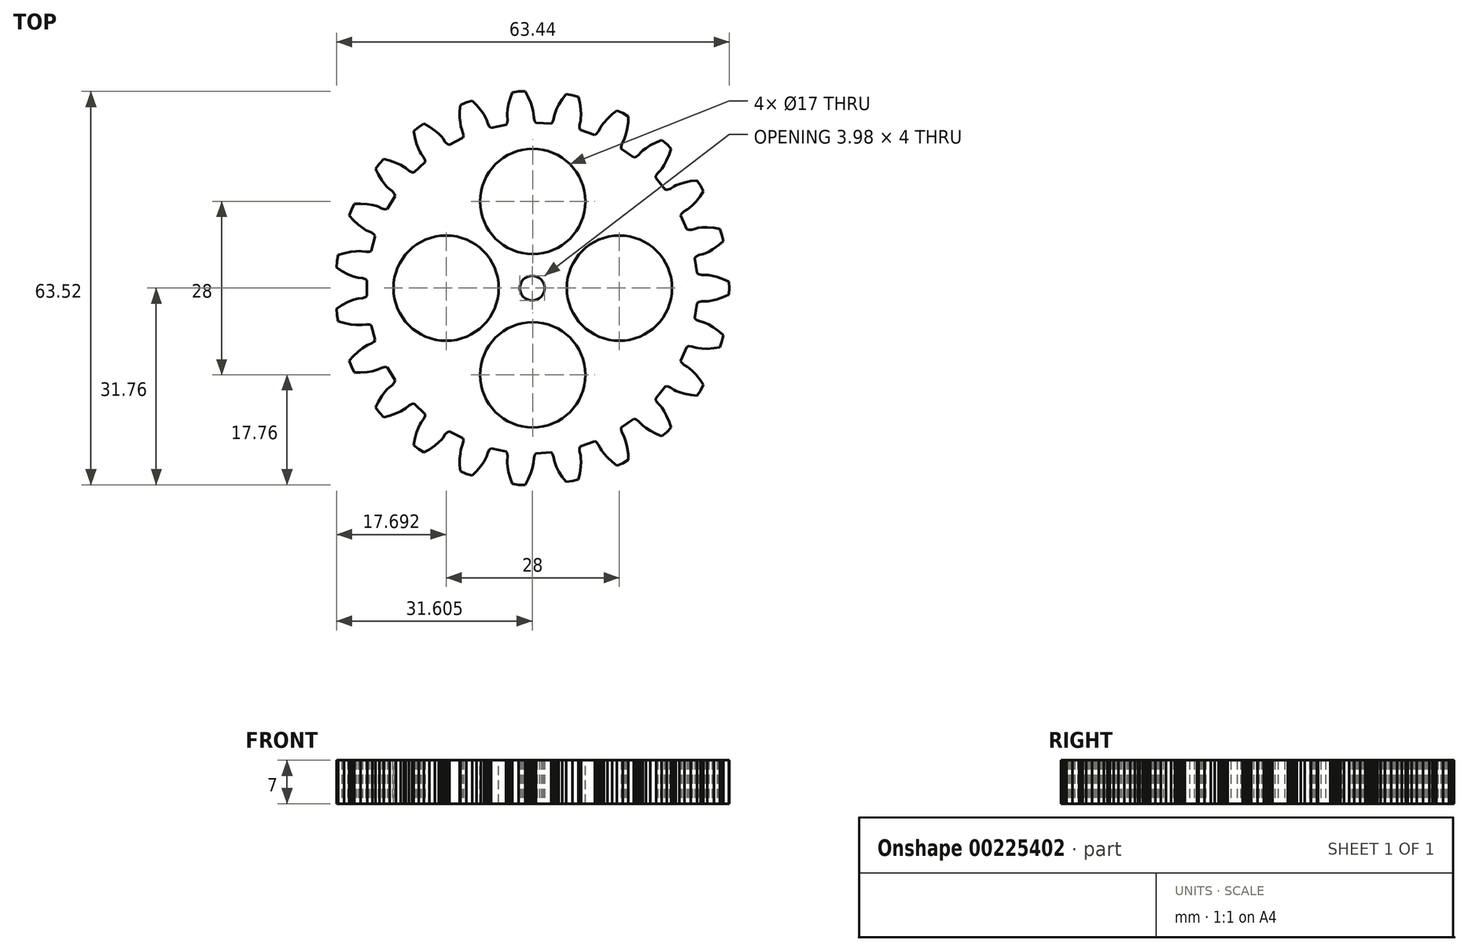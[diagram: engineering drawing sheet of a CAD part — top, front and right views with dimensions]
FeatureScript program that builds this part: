
annotation { "Feature Type Name" : "Feature", "Feature Type Description" : "" }
export const myFeature = defineFeature(function(context is Context, id is Id, definition is map)
    precondition{}
    {
        {
            var Q0;
            Q0=qCreatedBy(makeId("Top.planeOp"),FACE);
            var sketch = newSketch(context, id + "F0", { "sketchPlane" : qUnion([Q0])});
            skLineSegment(sketch, "E0", {"start": v(20.37, -9.56) * mm, "end": v(20.72, -8.59) * mm});
            skLineSegment(sketch, "E1", {"start": v(20.72, -8.59) * mm, "end": v(20.92, -7.58) * mm});
            skLineSegment(sketch, "E2", {"start": v(20.92, -7.58) * mm, "end": v(20.18, -6.94) * mm});
            skLineSegment(sketch, "E3", {"start": v(20.18, -6.94) * mm, "end": v(19.3, -6.31) * mm});
            skLineSegment(sketch, "E4", {"start": v(19.3, -6.31) * mm, "end": v(18.57, -5.89) * mm});
            skLineSegment(sketch, "E5", {"start": v(18.57, -5.89) * mm, "end": v(18.02, -5.63) * mm});
            skLineSegment(sketch, "E6", {"start": v(18.02, -5.63) * mm, "end": v(17.66, -5.5) * mm});
            skLineSegment(sketch, "E7", {"start": v(17.66, -5.5) * mm, "end": v(17.02, -5.34) * mm});
            skLineSegment(sketch, "E8", {"start": v(17.02, -5.34) * mm, "end": v(16.55, -5.1) * mm});
            skLineSegment(sketch, "E9", {"start": v(16.55, -5.1) * mm, "end": v(16.34, -4.85) * mm});
            skLineSegment(sketch, "E10", {"start": v(16.34, -4.85) * mm, "end": v(16.67, -2.42) * mm});
            skLineSegment(sketch, "E11", {"start": v(16.67, -2.42) * mm, "end": v(16.94, -2.23) * mm});
            skLineSegment(sketch, "E12", {"start": v(16.94, -2.23) * mm, "end": v(17.46, -2.14) * mm});
            skLineSegment(sketch, "E13", {"start": v(17.46, -2.14) * mm, "end": v(18.12, -2.15) * mm});
            skLineSegment(sketch, "E14", {"start": v(18.12, -2.15) * mm, "end": v(18.5, -2.12) * mm});
            skLineSegment(sketch, "E15", {"start": v(18.5, -2.12) * mm, "end": v(19.1, -2.02) * mm});
            skLineSegment(sketch, "E16", {"start": v(19.1, -2.02) * mm, "end": v(19.92, -1.8) * mm});
            skLineSegment(sketch, "E17", {"start": v(19.92, -1.8) * mm, "end": v(20.93, -1.45) * mm});
            skLineSegment(sketch, "E18", {"start": v(20.93, -1.45) * mm, "end": v(21.83, -1.03) * mm});
            skLineSegment(sketch, "E19", {"start": v(21.83, -1.03) * mm, "end": v(21.9, 0) * mm});
            skLineSegment(sketch, "E20", {"start": v(21.9, 0) * mm, "end": v(21.83, 1.03) * mm});
            skLineSegment(sketch, "E21", {"start": v(21.83, 1.03) * mm, "end": v(20.93, 1.45) * mm});
            skLineSegment(sketch, "E22", {"start": v(20.93, 1.45) * mm, "end": v(19.92, 1.8) * mm});
            skLineSegment(sketch, "E23", {"start": v(19.92, 1.8) * mm, "end": v(19.1, 2.02) * mm});
            skLineSegment(sketch, "E24", {"start": v(19.1, 2.02) * mm, "end": v(18.5, 2.12) * mm});
            skLineSegment(sketch, "E25", {"start": v(18.5, 2.12) * mm, "end": v(18.12, 2.15) * mm});
            skLineSegment(sketch, "E26", {"start": v(18.12, 2.15) * mm, "end": v(17.46, 2.14) * mm});
            skLineSegment(sketch, "E27", {"start": v(17.46, 2.14) * mm, "end": v(16.94, 2.23) * mm});
            skLineSegment(sketch, "E28", {"start": v(16.94, 2.23) * mm, "end": v(16.67, 2.42) * mm});
            skLineSegment(sketch, "E29", {"start": v(16.67, 2.42) * mm, "end": v(16.34, 4.85) * mm});
            skLineSegment(sketch, "E30", {"start": v(16.34, 4.85) * mm, "end": v(16.55, 5.1) * mm});
            skLineSegment(sketch, "E31", {"start": v(16.55, 5.1) * mm, "end": v(17.02, 5.34) * mm});
            skLineSegment(sketch, "E32", {"start": v(17.02, 5.34) * mm, "end": v(17.66, 5.5) * mm});
            skLineSegment(sketch, "E33", {"start": v(17.66, 5.5) * mm, "end": v(18.02, 5.63) * mm});
            skLineSegment(sketch, "E34", {"start": v(18.02, 5.63) * mm, "end": v(18.57, 5.89) * mm});
            skLineSegment(sketch, "E35", {"start": v(18.57, 5.89) * mm, "end": v(19.3, 6.31) * mm});
            skLineSegment(sketch, "E36", {"start": v(19.3, 6.31) * mm, "end": v(20.18, 6.94) * mm});
            skLineSegment(sketch, "E37", {"start": v(20.18, 6.94) * mm, "end": v(20.92, 7.58) * mm});
            skLineSegment(sketch, "E38", {"start": v(20.92, 7.58) * mm, "end": v(20.72, 8.59) * mm});
            skLineSegment(sketch, "E39", {"start": v(20.72, 8.59) * mm, "end": v(20.37, 9.56) * mm});
            skLineSegment(sketch, "E40", {"start": v(20.37, 9.56) * mm, "end": v(19.4, 9.72) * mm});
            skLineSegment(sketch, "E41", {"start": v(19.4, 9.72) * mm, "end": v(18.32, 9.8) * mm});
            skLineSegment(sketch, "E42", {"start": v(18.32, 9.8) * mm, "end": v(17.48, 9.78) * mm});
            skLineSegment(sketch, "E43", {"start": v(17.48, 9.78) * mm, "end": v(16.87, 9.71) * mm});
            skLineSegment(sketch, "E44", {"start": v(16.87, 9.71) * mm, "end": v(16.5, 9.64) * mm});
            skLineSegment(sketch, "E45", {"start": v(16.5, 9.64) * mm, "end": v(15.87, 9.45) * mm});
            skLineSegment(sketch, "E46", {"start": v(15.87, 9.45) * mm, "end": v(15.34, 9.4) * mm});
            skLineSegment(sketch, "E47", {"start": v(15.34, 9.4) * mm, "end": v(15.03, 9.5) * mm});
            skLineSegment(sketch, "E48", {"start": v(15.03, 9.5) * mm, "end": v(14.06, 11.76) * mm});
            skLineSegment(sketch, "E49", {"start": v(14.06, 11.76) * mm, "end": v(14.19, 12.06) * mm});
            skLineSegment(sketch, "E50", {"start": v(14.19, 12.06) * mm, "end": v(14.58, 12.41) * mm});
            skLineSegment(sketch, "E51", {"start": v(14.58, 12.41) * mm, "end": v(15.15, 12.74) * mm});
            skLineSegment(sketch, "E52", {"start": v(15.15, 12.74) * mm, "end": v(15.46, 12.96) * mm});
            skLineSegment(sketch, "E53", {"start": v(15.46, 12.96) * mm, "end": v(15.92, 13.36) * mm});
            skLineSegment(sketch, "E54", {"start": v(15.92, 13.36) * mm, "end": v(16.51, 13.97) * mm});
            skLineSegment(sketch, "E55", {"start": v(16.51, 13.97) * mm, "end": v(17.19, 14.8) * mm});
            skLineSegment(sketch, "E56", {"start": v(17.19, 14.8) * mm, "end": v(17.74, 15.62) * mm});
            skLineSegment(sketch, "E57", {"start": v(17.74, 15.62) * mm, "end": v(17.26, 16.54) * mm});
            skLineSegment(sketch, "E58", {"start": v(17.26, 16.54) * mm, "end": v(16.67, 17.38) * mm});
            skLineSegment(sketch, "E59", {"start": v(16.67, 17.38) * mm, "end": v(15.69, 17.27) * mm});
            skLineSegment(sketch, "E60", {"start": v(15.69, 17.27) * mm, "end": v(14.63, 17.06) * mm});
            skLineSegment(sketch, "E61", {"start": v(14.63, 17.06) * mm, "end": v(13.82, 16.81) * mm});
            skLineSegment(sketch, "E62", {"start": v(13.82, 16.81) * mm, "end": v(13.26, 16.59) * mm});
            skLineSegment(sketch, "E63", {"start": v(13.26, 16.59) * mm, "end": v(12.92, 16.41) * mm});
            skLineSegment(sketch, "E64", {"start": v(12.92, 16.41) * mm, "end": v(12.37, 16.06) * mm});
            skLineSegment(sketch, "E65", {"start": v(12.37, 16.06) * mm, "end": v(11.87, 15.87) * mm});
            skLineSegment(sketch, "E66", {"start": v(11.87, 15.87) * mm, "end": v(11.54, 15.9) * mm});
            skLineSegment(sketch, "E67", {"start": v(11.54, 15.9) * mm, "end": v(10, 17.8) * mm});
            skLineSegment(sketch, "E68", {"start": v(10, 17.8) * mm, "end": v(10.04, 18.12) * mm});
            skLineSegment(sketch, "E69", {"start": v(10.04, 18.12) * mm, "end": v(10.33, 18.57) * mm});
            skLineSegment(sketch, "E70", {"start": v(10.33, 18.57) * mm, "end": v(10.78, 19.04) * mm});
            skLineSegment(sketch, "E71", {"start": v(10.78, 19.04) * mm, "end": v(11.02, 19.33) * mm});
            skLineSegment(sketch, "E72", {"start": v(11.02, 19.33) * mm, "end": v(11.36, 19.84) * mm});
            skLineSegment(sketch, "E73", {"start": v(11.36, 19.84) * mm, "end": v(11.76, 20.58) * mm});
            skLineSegment(sketch, "E74", {"start": v(11.76, 20.58) * mm, "end": v(12.19, 21.57) * mm});
            skLineSegment(sketch, "E75", {"start": v(12.19, 21.57) * mm, "end": v(12.5, 22.51) * mm});
            skLineSegment(sketch, "E76", {"start": v(12.5, 22.51) * mm, "end": v(11.8, 23.26) * mm});
            skLineSegment(sketch, "E77", {"start": v(11.8, 23.26) * mm, "end": v(11, 23.91) * mm});
            skLineSegment(sketch, "E78", {"start": v(11, 23.91) * mm, "end": v(10.08, 23.54) * mm});
            skLineSegment(sketch, "E79", {"start": v(10.08, 23.54) * mm, "end": v(9.12, 23.05) * mm});
            skLineSegment(sketch, "E80", {"start": v(9.12, 23.05) * mm, "end": v(8.4, 22.6) * mm});
            skLineSegment(sketch, "E81", {"start": v(8.4, 22.6) * mm, "end": v(7.92, 22.23) * mm});
            skLineSegment(sketch, "E82", {"start": v(7.92, 22.23) * mm, "end": v(7.64, 21.97) * mm});
            skLineSegment(sketch, "E83", {"start": v(7.64, 21.97) * mm, "end": v(7.2, 21.48) * mm});
            skLineSegment(sketch, "E84", {"start": v(7.2, 21.48) * mm, "end": v(6.78, 21.17) * mm});
            skLineSegment(sketch, "E85", {"start": v(6.78, 21.17) * mm, "end": v(6.45, 21.1) * mm});
            skLineSegment(sketch, "E86", {"start": v(6.45, 21.1) * mm, "end": v(4.46, 22.5) * mm});
            skLineSegment(sketch, "E87", {"start": v(4.46, 22.5) * mm, "end": v(4.41, 22.84) * mm});
            skLineSegment(sketch, "E88", {"start": v(4.41, 22.84) * mm, "end": v(4.57, 23.34) * mm});
            skLineSegment(sketch, "E89", {"start": v(4.57, 23.34) * mm, "end": v(4.88, 23.92) * mm});
            skLineSegment(sketch, "E90", {"start": v(4.88, 23.92) * mm, "end": v(5.03, 24.27) * mm});
            skLineSegment(sketch, "E91", {"start": v(5.03, 24.27) * mm, "end": v(5.22, 24.85) * mm});
            skLineSegment(sketch, "E92", {"start": v(5.22, 24.85) * mm, "end": v(5.4, 25.67) * mm});
            skLineSegment(sketch, "E93", {"start": v(5.4, 25.67) * mm, "end": v(5.55, 26.74) * mm});
            skLineSegment(sketch, "E94", {"start": v(5.55, 26.74) * mm, "end": v(5.59, 27.73) * mm});
            skLineSegment(sketch, "E95", {"start": v(5.59, 27.73) * mm, "end": v(4.7, 28.26) * mm});
            skLineSegment(sketch, "E96", {"start": v(4.7, 28.26) * mm, "end": v(3.76, 28.67) * mm});
            skLineSegment(sketch, "E97", {"start": v(3.76, 28.67) * mm, "end": v(2.98, 28.07) * mm});
            skLineSegment(sketch, "E98", {"start": v(2.98, 28.07) * mm, "end": v(2.2, 27.34) * mm});
            skLineSegment(sketch, "E99", {"start": v(2.2, 27.34) * mm, "end": v(1.63, 26.71) * mm});
            skLineSegment(sketch, "E100", {"start": v(1.63, 26.71) * mm, "end": v(1.26, 26.22) * mm});
            skLineSegment(sketch, "E101", {"start": v(1.26, 26.22) * mm, "end": v(1.06, 25.9) * mm});
            skLineSegment(sketch, "E102", {"start": v(1.06, 25.9) * mm, "end": v(0.77, 25.3) * mm});
            skLineSegment(sketch, "E103", {"start": v(0.77, 25.3) * mm, "end": v(0.45, 24.9) * mm});
            skLineSegment(sketch, "E104", {"start": v(0.45, 24.9) * mm, "end": v(0.16, 24.74) * mm});
            skLineSegment(sketch, "E105", {"start": v(0.16, 24.74) * mm, "end": v(-2.15, 25.56) * mm});
            skLineSegment(sketch, "E106", {"start": v(-2.15, 25.56) * mm, "end": v(-2.28, 25.86) * mm});
            skLineSegment(sketch, "E107", {"start": v(-2.28, 25.86) * mm, "end": v(-2.27, 26.4) * mm});
            skLineSegment(sketch, "E108", {"start": v(-2.27, 26.4) * mm, "end": v(-2.12, 27.03) * mm});
            skLineSegment(sketch, "E109", {"start": v(-2.12, 27.03) * mm, "end": v(-2.07, 27.4) * mm});
            skLineSegment(sketch, "E110", {"start": v(-2.07, 27.4) * mm, "end": v(-2.05, 28.02) * mm});
            skLineSegment(sketch, "E111", {"start": v(-2.05, 28.02) * mm, "end": v(-2.1, 28.86) * mm});
            skLineSegment(sketch, "E112", {"start": v(-2.1, 28.86) * mm, "end": v(-2.24, 29.93) * mm});
            skLineSegment(sketch, "E113", {"start": v(-2.24, 29.93) * mm, "end": v(-2.47, 30.89) * mm});
            skLineSegment(sketch, "E114", {"start": v(-2.47, 30.89) * mm, "end": v(-3.46, 31.17) * mm});
            skLineSegment(sketch, "E115", {"start": v(-3.46, 31.17) * mm, "end": v(-4.48, 31.3) * mm});
            skLineSegment(sketch, "E116", {"start": v(-4.48, 31.3) * mm, "end": v(-5.07, 30.51) * mm});
            skLineSegment(sketch, "E117", {"start": v(-5.07, 30.51) * mm, "end": v(-5.63, 29.6) * mm});
            skLineSegment(sketch, "E118", {"start": v(-5.63, 29.6) * mm, "end": v(-6, 28.84) * mm});
            skLineSegment(sketch, "E119", {"start": v(-6, 28.84) * mm, "end": v(-6.23, 28.27) * mm});
            skLineSegment(sketch, "E120", {"start": v(-6.23, 28.27) * mm, "end": v(-6.33, 27.9) * mm});
            skLineSegment(sketch, "E121", {"start": v(-6.33, 27.9) * mm, "end": v(-6.45, 27.26) * mm});
            skLineSegment(sketch, "E122", {"start": v(-6.45, 27.26) * mm, "end": v(-6.65, 26.77) * mm});
            skLineSegment(sketch, "E123", {"start": v(-6.65, 26.77) * mm, "end": v(-6.9, 26.54) * mm});
            skLineSegment(sketch, "E124", {"start": v(-6.9, 26.54) * mm, "end": v(-9.34, 26.7) * mm});
            skLineSegment(sketch, "E125", {"start": v(-9.34, 26.7) * mm, "end": v(-9.54, 26.97) * mm});
            skLineSegment(sketch, "E126", {"start": v(-9.54, 26.97) * mm, "end": v(-9.67, 27.48) * mm});
            skLineSegment(sketch, "E127", {"start": v(-9.67, 27.48) * mm, "end": v(-9.7, 28.14) * mm});
            skLineSegment(sketch, "E128", {"start": v(-9.7, 28.14) * mm, "end": v(-9.76, 28.51) * mm});
            skLineSegment(sketch, "E129", {"start": v(-9.76, 28.51) * mm, "end": v(-9.9, 29.1) * mm});
            skLineSegment(sketch, "E130", {"start": v(-9.9, 29.1) * mm, "end": v(-10.17, 29.9) * mm});
            skLineSegment(sketch, "E131", {"start": v(-10.17, 29.9) * mm, "end": v(-10.6, 30.9) * mm});
            skLineSegment(sketch, "E132", {"start": v(-10.6, 30.9) * mm, "end": v(-11.08, 31.76) * mm});
            skLineSegment(sketch, "E133", {"start": v(-11.08, 31.76) * mm, "end": v(-12.1, 31.76) * mm});
            skLineSegment(sketch, "E134", {"start": v(-12.1, 31.76) * mm, "end": v(-13.13, 31.62) * mm});
            skLineSegment(sketch, "E135", {"start": v(-13.13, 31.62) * mm, "end": v(-13.48, 30.7) * mm});
            skLineSegment(sketch, "E136", {"start": v(-13.48, 30.7) * mm, "end": v(-13.78, 29.66) * mm});
            skLineSegment(sketch, "E137", {"start": v(-13.78, 29.66) * mm, "end": v(-13.93, 28.83) * mm});
            skLineSegment(sketch, "E138", {"start": v(-13.93, 28.83) * mm, "end": v(-14, 28.22) * mm});
            skLineSegment(sketch, "E139", {"start": v(-14, 28.22) * mm, "end": v(-14, 27.84) * mm});
            skLineSegment(sketch, "E140", {"start": v(-14, 27.84) * mm, "end": v(-13.94, 27.19) * mm});
            skLineSegment(sketch, "E141", {"start": v(-13.94, 27.19) * mm, "end": v(-14, 26.66) * mm});
            skLineSegment(sketch, "E142", {"start": v(-14, 26.66) * mm, "end": v(-14.17, 26.38) * mm});
            skLineSegment(sketch, "E143", {"start": v(-14.17, 26.38) * mm, "end": v(-16.56, 25.88) * mm});
            skLineSegment(sketch, "E144", {"start": v(-16.56, 25.88) * mm, "end": v(-16.83, 26.07) * mm});
            skLineSegment(sketch, "E145", {"start": v(-16.83, 26.07) * mm, "end": v(-17.1, 26.53) * mm});
            skLineSegment(sketch, "E146", {"start": v(-17.1, 26.53) * mm, "end": v(-17.3, 27.16) * mm});
            skLineSegment(sketch, "E147", {"start": v(-17.3, 27.16) * mm, "end": v(-17.46, 27.5) * mm});
            skLineSegment(sketch, "E148", {"start": v(-17.46, 27.5) * mm, "end": v(-17.75, 28.04) * mm});
            skLineSegment(sketch, "E149", {"start": v(-17.75, 28.04) * mm, "end": v(-18.23, 28.74) * mm});
            skLineSegment(sketch, "E150", {"start": v(-18.23, 28.74) * mm, "end": v(-18.91, 29.57) * mm});
            skLineSegment(sketch, "E151", {"start": v(-18.91, 29.57) * mm, "end": v(-19.6, 30.27) * mm});
            skLineSegment(sketch, "E152", {"start": v(-19.6, 30.27) * mm, "end": v(-20.6, 30) * mm});
            skLineSegment(sketch, "E153", {"start": v(-20.6, 30) * mm, "end": v(-21.54, 29.58) * mm});
            skLineSegment(sketch, "E154", {"start": v(-21.54, 29.58) * mm, "end": v(-21.63, 28.6) * mm});
            skLineSegment(sketch, "E155", {"start": v(-21.63, 28.6) * mm, "end": v(-21.64, 27.52) * mm});
            skLineSegment(sketch, "E156", {"start": v(-21.64, 27.52) * mm, "end": v(-21.56, 26.68) * mm});
            skLineSegment(sketch, "E157", {"start": v(-21.56, 26.68) * mm, "end": v(-21.46, 26.08) * mm});
            skLineSegment(sketch, "E158", {"start": v(-21.46, 26.08) * mm, "end": v(-21.35, 25.72) * mm});
            skLineSegment(sketch, "E159", {"start": v(-21.35, 25.72) * mm, "end": v(-21.12, 25.1) * mm});
            skLineSegment(sketch, "E160", {"start": v(-21.12, 25.1) * mm, "end": v(-21.04, 24.58) * mm});
            skLineSegment(sketch, "E161", {"start": v(-21.04, 24.58) * mm, "end": v(-21.13, 24.26) * mm});
            skLineSegment(sketch, "E162", {"start": v(-21.13, 24.26) * mm, "end": v(-23.3, 23.13) * mm});
            skLineSegment(sketch, "E163", {"start": v(-23.3, 23.13) * mm, "end": v(-23.61, 23.25) * mm});
            skLineSegment(sketch, "E164", {"start": v(-23.61, 23.25) * mm, "end": v(-24, 23.62) * mm});
            skLineSegment(sketch, "E165", {"start": v(-24, 23.62) * mm, "end": v(-24.36, 24.16) * mm});
            skLineSegment(sketch, "E166", {"start": v(-24.36, 24.16) * mm, "end": v(-24.6, 24.45) * mm});
            skLineSegment(sketch, "E167", {"start": v(-24.6, 24.45) * mm, "end": v(-25.03, 24.89) * mm});
            skLineSegment(sketch, "E168", {"start": v(-25.03, 24.89) * mm, "end": v(-25.67, 25.43) * mm});
            skLineSegment(sketch, "E169", {"start": v(-25.67, 25.43) * mm, "end": v(-26.55, 26.05) * mm});
            skLineSegment(sketch, "E170", {"start": v(-26.55, 26.05) * mm, "end": v(-27.41, 26.54) * mm});
            skLineSegment(sketch, "E171", {"start": v(-27.41, 26.54) * mm, "end": v(-28.3, 26) * mm});
            skLineSegment(sketch, "E172", {"start": v(-28.3, 26) * mm, "end": v(-29.1, 25.35) * mm});
            skLineSegment(sketch, "E173", {"start": v(-29.1, 25.35) * mm, "end": v(-28.92, 24.38) * mm});
            skLineSegment(sketch, "E174", {"start": v(-28.92, 24.38) * mm, "end": v(-28.63, 23.35) * mm});
            skLineSegment(sketch, "E175", {"start": v(-28.63, 23.35) * mm, "end": v(-28.33, 22.56) * mm});
            skLineSegment(sketch, "E176", {"start": v(-28.33, 22.56) * mm, "end": v(-28.07, 22) * mm});
            skLineSegment(sketch, "E177", {"start": v(-28.07, 22) * mm, "end": v(-27.87, 21.68) * mm});
            skLineSegment(sketch, "E178", {"start": v(-27.87, 21.68) * mm, "end": v(-27.48, 21.15) * mm});
            skLineSegment(sketch, "E179", {"start": v(-27.48, 21.15) * mm, "end": v(-27.26, 20.67) * mm});
            skLineSegment(sketch, "E180", {"start": v(-27.26, 20.67) * mm, "end": v(-27.26, 20.34) * mm});
            skLineSegment(sketch, "E181", {"start": v(-27.26, 20.34) * mm, "end": v(-29.05, 18.67) * mm});
            skLineSegment(sketch, "E182", {"start": v(-29.05, 18.67) * mm, "end": v(-29.38, 18.7) * mm});
            skLineSegment(sketch, "E183", {"start": v(-29.38, 18.7) * mm, "end": v(-29.84, 18.95) * mm});
            skLineSegment(sketch, "E184", {"start": v(-29.84, 18.95) * mm, "end": v(-30.34, 19.37) * mm});
            skLineSegment(sketch, "E185", {"start": v(-30.34, 19.37) * mm, "end": v(-30.65, 19.59) * mm});
            skLineSegment(sketch, "E186", {"start": v(-30.65, 19.59) * mm, "end": v(-31.18, 19.9) * mm});
            skLineSegment(sketch, "E187", {"start": v(-31.18, 19.9) * mm, "end": v(-31.95, 20.24) * mm});
            skLineSegment(sketch, "E188", {"start": v(-31.95, 20.24) * mm, "end": v(-32.97, 20.6) * mm});
            skLineSegment(sketch, "E189", {"start": v(-32.97, 20.6) * mm, "end": v(-33.92, 20.84) * mm});
            skLineSegment(sketch, "E190", {"start": v(-33.92, 20.84) * mm, "end": v(-34.63, 20.09) * mm});
            skLineSegment(sketch, "E191", {"start": v(-34.63, 20.09) * mm, "end": v(-35.22, 19.25) * mm});
            skLineSegment(sketch, "E192", {"start": v(-35.22, 19.25) * mm, "end": v(-34.8, 18.36) * mm});
            skLineSegment(sketch, "E193", {"start": v(-34.8, 18.36) * mm, "end": v(-34.24, 17.44) * mm});
            skLineSegment(sketch, "E194", {"start": v(-34.24, 17.44) * mm, "end": v(-33.74, 16.76) * mm});
            skLineSegment(sketch, "E195", {"start": v(-33.74, 16.76) * mm, "end": v(-33.33, 16.3) * mm});
            skLineSegment(sketch, "E196", {"start": v(-33.33, 16.3) * mm, "end": v(-33.05, 16.04) * mm});
            skLineSegment(sketch, "E197", {"start": v(-33.05, 16.04) * mm, "end": v(-32.54, 15.63) * mm});
            skLineSegment(sketch, "E198", {"start": v(-32.54, 15.63) * mm, "end": v(-32.2, 15.23) * mm});
            skLineSegment(sketch, "E199", {"start": v(-32.2, 15.23) * mm, "end": v(-32.1, 14.91) * mm});
            skLineSegment(sketch, "E200", {"start": v(-32.1, 14.91) * mm, "end": v(-33.37, 12.82) * mm});
            skLineSegment(sketch, "E201", {"start": v(-33.37, 12.82) * mm, "end": v(-33.7, 12.76) * mm});
            skLineSegment(sketch, "E202", {"start": v(-33.7, 12.76) * mm, "end": v(-34.22, 12.87) * mm});
            skLineSegment(sketch, "E203", {"start": v(-34.22, 12.87) * mm, "end": v(-34.81, 13.15) * mm});
            skLineSegment(sketch, "E204", {"start": v(-34.81, 13.15) * mm, "end": v(-35.17, 13.27) * mm});
            skLineSegment(sketch, "E205", {"start": v(-35.17, 13.27) * mm, "end": v(-35.76, 13.42) * mm});
            skLineSegment(sketch, "E206", {"start": v(-35.76, 13.42) * mm, "end": v(-36.6, 13.55) * mm});
            skLineSegment(sketch, "E207", {"start": v(-36.6, 13.55) * mm, "end": v(-37.67, 13.62) * mm});
            skLineSegment(sketch, "E208", {"start": v(-37.67, 13.62) * mm, "end": v(-38.66, 13.6) * mm});
            skLineSegment(sketch, "E209", {"start": v(-38.66, 13.6) * mm, "end": v(-39.13, 12.68) * mm});
            skLineSegment(sketch, "E210", {"start": v(-39.13, 12.68) * mm, "end": v(-39.48, 11.71) * mm});
            skLineSegment(sketch, "E211", {"start": v(-39.48, 11.71) * mm, "end": v(-38.82, 10.97) * mm});
            skLineSegment(sketch, "E212", {"start": v(-38.82, 10.97) * mm, "end": v(-38.04, 10.23) * mm});
            skLineSegment(sketch, "E213", {"start": v(-38.04, 10.23) * mm, "end": v(-37.37, 9.71) * mm});
            skLineSegment(sketch, "E214", {"start": v(-37.37, 9.71) * mm, "end": v(-36.86, 9.38) * mm});
            skLineSegment(sketch, "E215", {"start": v(-36.86, 9.38) * mm, "end": v(-36.52, 9.2) * mm});
            skLineSegment(sketch, "E216", {"start": v(-36.52, 9.2) * mm, "end": v(-35.92, 8.96) * mm});
            skLineSegment(sketch, "E217", {"start": v(-35.92, 8.96) * mm, "end": v(-35.48, 8.66) * mm});
            skLineSegment(sketch, "E218", {"start": v(-35.48, 8.66) * mm, "end": v(-35.3, 8.38) * mm});
            skLineSegment(sketch, "E219", {"start": v(-35.3, 8.38) * mm, "end": v(-35.96, 6.02) * mm});
            skLineSegment(sketch, "E220", {"start": v(-35.96, 6.02) * mm, "end": v(-36.26, 5.87) * mm});
            skLineSegment(sketch, "E221", {"start": v(-36.26, 5.87) * mm, "end": v(-36.79, 5.85) * mm});
            skLineSegment(sketch, "E222", {"start": v(-36.79, 5.85) * mm, "end": v(-37.44, 5.95) * mm});
            skLineSegment(sketch, "E223", {"start": v(-37.44, 5.95) * mm, "end": v(-37.82, 5.97) * mm});
            skLineSegment(sketch, "E224", {"start": v(-37.82, 5.97) * mm, "end": v(-38.43, 5.96) * mm});
            skLineSegment(sketch, "E225", {"start": v(-38.43, 5.96) * mm, "end": v(-39.26, 5.86) * mm});
            skLineSegment(sketch, "E226", {"start": v(-39.26, 5.86) * mm, "end": v(-40.32, 5.63) * mm});
            skLineSegment(sketch, "E227", {"start": v(-40.32, 5.63) * mm, "end": v(-41.26, 5.34) * mm});
            skLineSegment(sketch, "E228", {"start": v(-41.26, 5.34) * mm, "end": v(-41.47, 4.33) * mm});
            skLineSegment(sketch, "E229", {"start": v(-41.47, 4.33) * mm, "end": v(-41.54, 3.3) * mm});
            skLineSegment(sketch, "E230", {"start": v(-41.54, 3.3) * mm, "end": v(-40.71, 2.77) * mm});
            skLineSegment(sketch, "E231", {"start": v(-40.71, 2.77) * mm, "end": v(-39.76, 2.27) * mm});
            skLineSegment(sketch, "E232", {"start": v(-39.76, 2.27) * mm, "end": v(-38.98, 1.95) * mm});
            skLineSegment(sketch, "E233", {"start": v(-38.98, 1.95) * mm, "end": v(-38.4, 1.77) * mm});
            skLineSegment(sketch, "E234", {"start": v(-38.4, 1.77) * mm, "end": v(-38.02, 1.7) * mm});
            skLineSegment(sketch, "E235", {"start": v(-38.02, 1.7) * mm, "end": v(-37.37, 1.62) * mm});
            skLineSegment(sketch, "E236", {"start": v(-37.37, 1.62) * mm, "end": v(-36.87, 1.45) * mm});
            skLineSegment(sketch, "E237", {"start": v(-36.87, 1.45) * mm, "end": v(-36.62, 1.22) * mm});
            skLineSegment(sketch, "E238", {"start": v(-36.62, 1.22) * mm, "end": v(-36.62, -1.22) * mm});
            skLineSegment(sketch, "E239", {"start": v(-36.62, -1.22) * mm, "end": v(-36.87, -1.45) * mm});
            skLineSegment(sketch, "E240", {"start": v(-36.87, -1.45) * mm, "end": v(-37.37, -1.62) * mm});
            skLineSegment(sketch, "E241", {"start": v(-37.37, -1.62) * mm, "end": v(-38.02, -1.7) * mm});
            skLineSegment(sketch, "E242", {"start": v(-38.02, -1.7) * mm, "end": v(-38.4, -1.77) * mm});
            skLineSegment(sketch, "E243", {"start": v(-38.4, -1.77) * mm, "end": v(-38.98, -1.95) * mm});
            skLineSegment(sketch, "E244", {"start": v(-38.98, -1.95) * mm, "end": v(-39.76, -2.27) * mm});
            skLineSegment(sketch, "E245", {"start": v(-39.76, -2.27) * mm, "end": v(-40.71, -2.77) * mm});
            skLineSegment(sketch, "E246", {"start": v(-40.71, -2.77) * mm, "end": v(-41.54, -3.3) * mm});
            skLineSegment(sketch, "E247", {"start": v(-41.54, -3.3) * mm, "end": v(-41.47, -4.33) * mm});
            skLineSegment(sketch, "E248", {"start": v(-41.47, -4.33) * mm, "end": v(-41.26, -5.34) * mm});
            skLineSegment(sketch, "E249", {"start": v(-41.26, -5.34) * mm, "end": v(-40.32, -5.63) * mm});
            skLineSegment(sketch, "E250", {"start": v(-40.32, -5.63) * mm, "end": v(-39.26, -5.86) * mm});
            skLineSegment(sketch, "E251", {"start": v(-39.26, -5.86) * mm, "end": v(-38.43, -5.96) * mm});
            skLineSegment(sketch, "E252", {"start": v(-38.43, -5.96) * mm, "end": v(-37.82, -5.97) * mm});
            skLineSegment(sketch, "E253", {"start": v(-37.82, -5.97) * mm, "end": v(-37.44, -5.95) * mm});
            skLineSegment(sketch, "E254", {"start": v(-37.44, -5.95) * mm, "end": v(-36.79, -5.85) * mm});
            skLineSegment(sketch, "E255", {"start": v(-36.79, -5.85) * mm, "end": v(-36.26, -5.87) * mm});
            skLineSegment(sketch, "E256", {"start": v(-36.26, -5.87) * mm, "end": v(-35.96, -6.02) * mm});
            skLineSegment(sketch, "E257", {"start": v(-35.96, -6.02) * mm, "end": v(-35.3, -8.38) * mm});
            skLineSegment(sketch, "E258", {"start": v(-35.3, -8.38) * mm, "end": v(-35.48, -8.66) * mm});
            skLineSegment(sketch, "E259", {"start": v(-35.48, -8.66) * mm, "end": v(-35.92, -8.96) * mm});
            skLineSegment(sketch, "E260", {"start": v(-35.92, -8.96) * mm, "end": v(-36.52, -9.2) * mm});
            skLineSegment(sketch, "E261", {"start": v(-36.52, -9.2) * mm, "end": v(-36.86, -9.38) * mm});
            skLineSegment(sketch, "E262", {"start": v(-36.86, -9.38) * mm, "end": v(-37.37, -9.71) * mm});
            skLineSegment(sketch, "E263", {"start": v(-37.37, -9.71) * mm, "end": v(-38.04, -10.23) * mm});
            skLineSegment(sketch, "E264", {"start": v(-38.04, -10.23) * mm, "end": v(-38.82, -10.97) * mm});
            skLineSegment(sketch, "E265", {"start": v(-38.82, -10.97) * mm, "end": v(-39.48, -11.71) * mm});
            skLineSegment(sketch, "E266", {"start": v(-39.48, -11.71) * mm, "end": v(-39.13, -12.68) * mm});
            skLineSegment(sketch, "E267", {"start": v(-39.13, -12.68) * mm, "end": v(-38.66, -13.6) * mm});
            skLineSegment(sketch, "E268", {"start": v(-38.66, -13.6) * mm, "end": v(-37.67, -13.62) * mm});
            skLineSegment(sketch, "E269", {"start": v(-37.67, -13.62) * mm, "end": v(-36.6, -13.55) * mm});
            skLineSegment(sketch, "E270", {"start": v(-36.6, -13.55) * mm, "end": v(-35.76, -13.42) * mm});
            skLineSegment(sketch, "E271", {"start": v(-35.76, -13.42) * mm, "end": v(-35.17, -13.27) * mm});
            skLineSegment(sketch, "E272", {"start": v(-35.17, -13.27) * mm, "end": v(-34.81, -13.15) * mm});
            skLineSegment(sketch, "E273", {"start": v(-34.81, -13.15) * mm, "end": v(-34.22, -12.87) * mm});
            skLineSegment(sketch, "E274", {"start": v(-34.22, -12.87) * mm, "end": v(-33.7, -12.76) * mm});
            skLineSegment(sketch, "E275", {"start": v(-33.7, -12.76) * mm, "end": v(-33.37, -12.82) * mm});
            skLineSegment(sketch, "E276", {"start": v(-33.37, -12.82) * mm, "end": v(-32.1, -14.91) * mm});
            skLineSegment(sketch, "E277", {"start": v(-32.1, -14.91) * mm, "end": v(-32.2, -15.23) * mm});
            skLineSegment(sketch, "E278", {"start": v(-32.2, -15.23) * mm, "end": v(-32.54, -15.63) * mm});
            skLineSegment(sketch, "E279", {"start": v(-32.54, -15.63) * mm, "end": v(-33.05, -16.04) * mm});
            skLineSegment(sketch, "E280", {"start": v(-33.05, -16.04) * mm, "end": v(-33.33, -16.3) * mm});
            skLineSegment(sketch, "E281", {"start": v(-33.33, -16.3) * mm, "end": v(-33.74, -16.76) * mm});
            skLineSegment(sketch, "E282", {"start": v(-33.74, -16.76) * mm, "end": v(-34.24, -17.44) * mm});
            skLineSegment(sketch, "E283", {"start": v(-34.24, -17.44) * mm, "end": v(-34.8, -18.36) * mm});
            skLineSegment(sketch, "E284", {"start": v(-34.8, -18.36) * mm, "end": v(-35.22, -19.25) * mm});
            skLineSegment(sketch, "E285", {"start": v(-35.22, -19.25) * mm, "end": v(-34.63, -20.09) * mm});
            skLineSegment(sketch, "E286", {"start": v(-34.63, -20.09) * mm, "end": v(-33.92, -20.84) * mm});
            skLineSegment(sketch, "E287", {"start": v(-33.92, -20.84) * mm, "end": v(-32.97, -20.6) * mm});
            skLineSegment(sketch, "E288", {"start": v(-32.97, -20.6) * mm, "end": v(-31.95, -20.24) * mm});
            skLineSegment(sketch, "E289", {"start": v(-31.95, -20.24) * mm, "end": v(-31.18, -19.9) * mm});
            skLineSegment(sketch, "E290", {"start": v(-31.18, -19.9) * mm, "end": v(-30.65, -19.59) * mm});
            skLineSegment(sketch, "E291", {"start": v(-30.65, -19.59) * mm, "end": v(-30.34, -19.37) * mm});
            skLineSegment(sketch, "E292", {"start": v(-30.34, -19.37) * mm, "end": v(-29.84, -18.95) * mm});
            skLineSegment(sketch, "E293", {"start": v(-29.84, -18.95) * mm, "end": v(-29.38, -18.7) * mm});
            skLineSegment(sketch, "E294", {"start": v(-29.38, -18.7) * mm, "end": v(-29.05, -18.67) * mm});
            skLineSegment(sketch, "E295", {"start": v(-29.05, -18.67) * mm, "end": v(-27.26, -20.34) * mm});
            skLineSegment(sketch, "E296", {"start": v(-27.26, -20.34) * mm, "end": v(-27.26, -20.67) * mm});
            skLineSegment(sketch, "E297", {"start": v(-27.26, -20.67) * mm, "end": v(-27.48, -21.15) * mm});
            skLineSegment(sketch, "E298", {"start": v(-27.48, -21.15) * mm, "end": v(-27.87, -21.68) * mm});
            skLineSegment(sketch, "E299", {"start": v(-27.87, -21.68) * mm, "end": v(-28.07, -22) * mm});
            skLineSegment(sketch, "E300", {"start": v(-28.07, -22) * mm, "end": v(-28.33, -22.56) * mm});
            skLineSegment(sketch, "E301", {"start": v(-28.33, -22.56) * mm, "end": v(-28.63, -23.35) * mm});
            skLineSegment(sketch, "E302", {"start": v(-28.63, -23.35) * mm, "end": v(-28.92, -24.38) * mm});
            skLineSegment(sketch, "E303", {"start": v(-28.92, -24.38) * mm, "end": v(-29.1, -25.35) * mm});
            skLineSegment(sketch, "E304", {"start": v(-29.1, -25.35) * mm, "end": v(-28.3, -26) * mm});
            skLineSegment(sketch, "E305", {"start": v(-28.3, -26) * mm, "end": v(-27.41, -26.54) * mm});
            skLineSegment(sketch, "E306", {"start": v(-27.41, -26.54) * mm, "end": v(-26.55, -26.05) * mm});
            skLineSegment(sketch, "E307", {"start": v(-26.55, -26.05) * mm, "end": v(-25.67, -25.43) * mm});
            skLineSegment(sketch, "E308", {"start": v(-25.67, -25.43) * mm, "end": v(-25.03, -24.89) * mm});
            skLineSegment(sketch, "E309", {"start": v(-25.03, -24.89) * mm, "end": v(-24.6, -24.45) * mm});
            skLineSegment(sketch, "E310", {"start": v(-24.6, -24.45) * mm, "end": v(-24.36, -24.16) * mm});
            skLineSegment(sketch, "E311", {"start": v(-24.36, -24.16) * mm, "end": v(-24, -23.62) * mm});
            skLineSegment(sketch, "E312", {"start": v(-24, -23.62) * mm, "end": v(-23.61, -23.25) * mm});
            skLineSegment(sketch, "E313", {"start": v(-23.61, -23.25) * mm, "end": v(-23.3, -23.13) * mm});
            skLineSegment(sketch, "E314", {"start": v(-23.3, -23.13) * mm, "end": v(-21.13, -24.26) * mm});
            skLineSegment(sketch, "E315", {"start": v(-21.13, -24.26) * mm, "end": v(-21.04, -24.58) * mm});
            skLineSegment(sketch, "E316", {"start": v(-21.04, -24.58) * mm, "end": v(-21.12, -25.1) * mm});
            skLineSegment(sketch, "E317", {"start": v(-21.12, -25.1) * mm, "end": v(-21.35, -25.72) * mm});
            skLineSegment(sketch, "E318", {"start": v(-21.35, -25.72) * mm, "end": v(-21.46, -26.08) * mm});
            skLineSegment(sketch, "E319", {"start": v(-21.46, -26.08) * mm, "end": v(-21.56, -26.68) * mm});
            skLineSegment(sketch, "E320", {"start": v(-21.56, -26.68) * mm, "end": v(-21.64, -27.52) * mm});
            skLineSegment(sketch, "E321", {"start": v(-21.64, -27.52) * mm, "end": v(-21.63, -28.6) * mm});
            skLineSegment(sketch, "E322", {"start": v(-21.63, -28.6) * mm, "end": v(-21.54, -29.58) * mm});
            skLineSegment(sketch, "E323", {"start": v(-21.54, -29.58) * mm, "end": v(-20.6, -30) * mm});
            skLineSegment(sketch, "E324", {"start": v(-20.6, -30) * mm, "end": v(-19.6, -30.27) * mm});
            skLineSegment(sketch, "E325", {"start": v(-19.6, -30.27) * mm, "end": v(-18.91, -29.57) * mm});
            skLineSegment(sketch, "E326", {"start": v(-18.91, -29.57) * mm, "end": v(-18.23, -28.74) * mm});
            skLineSegment(sketch, "E327", {"start": v(-18.23, -28.74) * mm, "end": v(-17.75, -28.04) * mm});
            skLineSegment(sketch, "E328", {"start": v(-17.75, -28.04) * mm, "end": v(-17.46, -27.5) * mm});
            skLineSegment(sketch, "E329", {"start": v(-17.46, -27.5) * mm, "end": v(-17.3, -27.16) * mm});
            skLineSegment(sketch, "E330", {"start": v(-17.3, -27.16) * mm, "end": v(-17.1, -26.53) * mm});
            skLineSegment(sketch, "E331", {"start": v(-17.1, -26.53) * mm, "end": v(-16.83, -26.07) * mm});
            skLineSegment(sketch, "E332", {"start": v(-16.83, -26.07) * mm, "end": v(-16.56, -25.88) * mm});
            skLineSegment(sketch, "E333", {"start": v(-16.56, -25.88) * mm, "end": v(-14.17, -26.38) * mm});
            skLineSegment(sketch, "E334", {"start": v(-14.17, -26.38) * mm, "end": v(-14, -26.66) * mm});
            skLineSegment(sketch, "E335", {"start": v(-14, -26.66) * mm, "end": v(-13.94, -27.19) * mm});
            skLineSegment(sketch, "E336", {"start": v(-13.94, -27.19) * mm, "end": v(-14, -27.84) * mm});
            skLineSegment(sketch, "E337", {"start": v(-14, -27.84) * mm, "end": v(-14, -28.22) * mm});
            skLineSegment(sketch, "E338", {"start": v(-14, -28.22) * mm, "end": v(-13.93, -28.83) * mm});
            skLineSegment(sketch, "E339", {"start": v(-13.93, -28.83) * mm, "end": v(-13.78, -29.66) * mm});
            skLineSegment(sketch, "E340", {"start": v(-13.78, -29.66) * mm, "end": v(-13.48, -30.7) * mm});
            skLineSegment(sketch, "E341", {"start": v(-13.48, -30.7) * mm, "end": v(-13.13, -31.62) * mm});
            skLineSegment(sketch, "E342", {"start": v(-13.13, -31.62) * mm, "end": v(-12.1, -31.76) * mm});
            skLineSegment(sketch, "E343", {"start": v(-12.1, -31.76) * mm, "end": v(-11.08, -31.76) * mm});
            skLineSegment(sketch, "E344", {"start": v(-11.08, -31.76) * mm, "end": v(-10.6, -30.9) * mm});
            skLineSegment(sketch, "E345", {"start": v(-10.6, -30.9) * mm, "end": v(-10.17, -29.9) * mm});
            skLineSegment(sketch, "E346", {"start": v(-10.17, -29.9) * mm, "end": v(-9.9, -29.1) * mm});
            skLineSegment(sketch, "E347", {"start": v(-9.9, -29.1) * mm, "end": v(-9.76, -28.51) * mm});
            skLineSegment(sketch, "E348", {"start": v(-9.76, -28.51) * mm, "end": v(-9.7, -28.14) * mm});
            skLineSegment(sketch, "E349", {"start": v(-9.7, -28.14) * mm, "end": v(-9.67, -27.48) * mm});
            skLineSegment(sketch, "E350", {"start": v(-9.67, -27.48) * mm, "end": v(-9.54, -26.97) * mm});
            skLineSegment(sketch, "E351", {"start": v(-9.54, -26.97) * mm, "end": v(-9.34, -26.7) * mm});
            skLineSegment(sketch, "E352", {"start": v(-9.34, -26.7) * mm, "end": v(-6.9, -26.54) * mm});
            skLineSegment(sketch, "E353", {"start": v(-6.9, -26.54) * mm, "end": v(-6.65, -26.77) * mm});
            skLineSegment(sketch, "E354", {"start": v(-6.65, -26.77) * mm, "end": v(-6.45, -27.26) * mm});
            skLineSegment(sketch, "E355", {"start": v(-6.45, -27.26) * mm, "end": v(-6.33, -27.9) * mm});
            skLineSegment(sketch, "E356", {"start": v(-6.33, -27.9) * mm, "end": v(-6.23, -28.27) * mm});
            skLineSegment(sketch, "E357", {"start": v(-6.23, -28.27) * mm, "end": v(-6, -28.84) * mm});
            skLineSegment(sketch, "E358", {"start": v(-6, -28.84) * mm, "end": v(-5.63, -29.6) * mm});
            skLineSegment(sketch, "E359", {"start": v(-5.63, -29.6) * mm, "end": v(-5.07, -30.51) * mm});
            skLineSegment(sketch, "E360", {"start": v(-5.07, -30.51) * mm, "end": v(-4.48, -31.3) * mm});
            skLineSegment(sketch, "E361", {"start": v(-4.48, -31.3) * mm, "end": v(-3.46, -31.17) * mm});
            skLineSegment(sketch, "E362", {"start": v(-3.46, -31.17) * mm, "end": v(-2.47, -30.89) * mm});
            skLineSegment(sketch, "E363", {"start": v(-2.47, -30.89) * mm, "end": v(-2.24, -29.93) * mm});
            skLineSegment(sketch, "E364", {"start": v(-2.24, -29.93) * mm, "end": v(-2.1, -28.86) * mm});
            skLineSegment(sketch, "E365", {"start": v(-2.1, -28.86) * mm, "end": v(-2.05, -28.02) * mm});
            skLineSegment(sketch, "E366", {"start": v(-2.05, -28.02) * mm, "end": v(-2.07, -27.4) * mm});
            skLineSegment(sketch, "E367", {"start": v(-2.07, -27.4) * mm, "end": v(-2.12, -27.03) * mm});
            skLineSegment(sketch, "E368", {"start": v(-2.12, -27.03) * mm, "end": v(-2.27, -26.4) * mm});
            skLineSegment(sketch, "E369", {"start": v(-2.27, -26.4) * mm, "end": v(-2.28, -25.86) * mm});
            skLineSegment(sketch, "E370", {"start": v(-2.28, -25.86) * mm, "end": v(-2.15, -25.56) * mm});
            skLineSegment(sketch, "E371", {"start": v(-2.15, -25.56) * mm, "end": v(0.16, -24.74) * mm});
            skLineSegment(sketch, "E372", {"start": v(0.16, -24.74) * mm, "end": v(0.45, -24.9) * mm});
            skLineSegment(sketch, "E373", {"start": v(0.45, -24.9) * mm, "end": v(0.77, -25.3) * mm});
            skLineSegment(sketch, "E374", {"start": v(0.77, -25.3) * mm, "end": v(1.06, -25.9) * mm});
            skLineSegment(sketch, "E375", {"start": v(1.06, -25.9) * mm, "end": v(1.26, -26.22) * mm});
            skLineSegment(sketch, "E376", {"start": v(1.26, -26.22) * mm, "end": v(1.63, -26.71) * mm});
            skLineSegment(sketch, "E377", {"start": v(1.63, -26.71) * mm, "end": v(2.2, -27.34) * mm});
            skLineSegment(sketch, "E378", {"start": v(2.2, -27.34) * mm, "end": v(2.98, -28.07) * mm});
            skLineSegment(sketch, "E379", {"start": v(2.98, -28.07) * mm, "end": v(3.76, -28.67) * mm});
            skLineSegment(sketch, "E380", {"start": v(3.76, -28.67) * mm, "end": v(4.7, -28.26) * mm});
            skLineSegment(sketch, "E381", {"start": v(4.7, -28.26) * mm, "end": v(5.59, -27.73) * mm});
            skLineSegment(sketch, "E382", {"start": v(5.59, -27.73) * mm, "end": v(5.55, -26.74) * mm});
            skLineSegment(sketch, "E383", {"start": v(5.55, -26.74) * mm, "end": v(5.4, -25.67) * mm});
            skLineSegment(sketch, "E384", {"start": v(5.4, -25.67) * mm, "end": v(5.22, -24.85) * mm});
            skLineSegment(sketch, "E385", {"start": v(5.22, -24.85) * mm, "end": v(5.03, -24.27) * mm});
            skLineSegment(sketch, "E386", {"start": v(5.03, -24.27) * mm, "end": v(4.88, -23.92) * mm});
            skLineSegment(sketch, "E387", {"start": v(4.88, -23.92) * mm, "end": v(4.57, -23.34) * mm});
            skLineSegment(sketch, "E388", {"start": v(4.57, -23.34) * mm, "end": v(4.41, -22.84) * mm});
            skLineSegment(sketch, "E389", {"start": v(4.41, -22.84) * mm, "end": v(4.46, -22.5) * mm});
            skLineSegment(sketch, "E390", {"start": v(4.46, -22.5) * mm, "end": v(6.45, -21.1) * mm});
            skLineSegment(sketch, "E391", {"start": v(6.45, -21.1) * mm, "end": v(6.78, -21.17) * mm});
            skLineSegment(sketch, "E392", {"start": v(6.78, -21.17) * mm, "end": v(7.2, -21.48) * mm});
            skLineSegment(sketch, "E393", {"start": v(7.2, -21.48) * mm, "end": v(7.64, -21.97) * mm});
            skLineSegment(sketch, "E394", {"start": v(7.64, -21.97) * mm, "end": v(7.92, -22.23) * mm});
            skLineSegment(sketch, "E395", {"start": v(7.92, -22.23) * mm, "end": v(8.4, -22.6) * mm});
            skLineSegment(sketch, "E396", {"start": v(8.4, -22.6) * mm, "end": v(9.12, -23.05) * mm});
            skLineSegment(sketch, "E397", {"start": v(9.12, -23.05) * mm, "end": v(10.08, -23.54) * mm});
            skLineSegment(sketch, "E398", {"start": v(10.08, -23.54) * mm, "end": v(11, -23.91) * mm});
            skLineSegment(sketch, "E399", {"start": v(11, -23.91) * mm, "end": v(11.8, -23.26) * mm});
            skLineSegment(sketch, "E400", {"start": v(11.8, -23.26) * mm, "end": v(12.5, -22.51) * mm});
            skLineSegment(sketch, "E401", {"start": v(12.5, -22.51) * mm, "end": v(12.19, -21.57) * mm});
            skLineSegment(sketch, "E402", {"start": v(12.19, -21.57) * mm, "end": v(11.76, -20.58) * mm});
            skLineSegment(sketch, "E403", {"start": v(11.76, -20.58) * mm, "end": v(11.36, -19.84) * mm});
            skLineSegment(sketch, "E404", {"start": v(11.36, -19.84) * mm, "end": v(11.02, -19.33) * mm});
            skLineSegment(sketch, "E405", {"start": v(11.02, -19.33) * mm, "end": v(10.78, -19.04) * mm});
            skLineSegment(sketch, "E406", {"start": v(10.78, -19.04) * mm, "end": v(10.33, -18.57) * mm});
            skLineSegment(sketch, "E407", {"start": v(10.33, -18.57) * mm, "end": v(10.04, -18.12) * mm});
            skLineSegment(sketch, "E408", {"start": v(10.04, -18.12) * mm, "end": v(10, -17.8) * mm});
            skLineSegment(sketch, "E409", {"start": v(10, -17.8) * mm, "end": v(11.54, -15.9) * mm});
            skLineSegment(sketch, "E410", {"start": v(11.54, -15.9) * mm, "end": v(11.87, -15.87) * mm});
            skLineSegment(sketch, "E411", {"start": v(11.87, -15.87) * mm, "end": v(12.37, -16.06) * mm});
            skLineSegment(sketch, "E412", {"start": v(12.37, -16.06) * mm, "end": v(12.92, -16.41) * mm});
            skLineSegment(sketch, "E413", {"start": v(12.92, -16.41) * mm, "end": v(13.26, -16.59) * mm});
            skLineSegment(sketch, "E414", {"start": v(13.26, -16.59) * mm, "end": v(13.82, -16.81) * mm});
            skLineSegment(sketch, "E415", {"start": v(13.82, -16.81) * mm, "end": v(14.63, -17.06) * mm});
            skLineSegment(sketch, "E416", {"start": v(14.63, -17.06) * mm, "end": v(15.69, -17.27) * mm});
            skLineSegment(sketch, "E417", {"start": v(15.69, -17.27) * mm, "end": v(16.67, -17.38) * mm});
            skLineSegment(sketch, "E418", {"start": v(16.67, -17.38) * mm, "end": v(17.26, -16.54) * mm});
            skLineSegment(sketch, "E419", {"start": v(17.26, -16.54) * mm, "end": v(17.74, -15.62) * mm});
            skLineSegment(sketch, "E420", {"start": v(17.74, -15.62) * mm, "end": v(17.19, -14.8) * mm});
            skLineSegment(sketch, "E421", {"start": v(17.19, -14.8) * mm, "end": v(16.51, -13.97) * mm});
            skLineSegment(sketch, "E422", {"start": v(16.51, -13.97) * mm, "end": v(15.92, -13.36) * mm});
            skLineSegment(sketch, "E423", {"start": v(15.92, -13.36) * mm, "end": v(15.46, -12.96) * mm});
            skLineSegment(sketch, "E424", {"start": v(15.46, -12.96) * mm, "end": v(15.15, -12.74) * mm});
            skLineSegment(sketch, "E425", {"start": v(15.15, -12.74) * mm, "end": v(14.58, -12.41) * mm});
            skLineSegment(sketch, "E426", {"start": v(14.58, -12.41) * mm, "end": v(14.19, -12.06) * mm});
            skLineSegment(sketch, "E427", {"start": v(14.19, -12.06) * mm, "end": v(14.06, -11.76) * mm});
            skLineSegment(sketch, "E428", {"start": v(14.06, -11.76) * mm, "end": v(15.03, -9.5) * mm});
            skLineSegment(sketch, "E429", {"start": v(15.03, -9.5) * mm, "end": v(15.34, -9.4) * mm});
            skLineSegment(sketch, "E430", {"start": v(15.34, -9.4) * mm, "end": v(15.87, -9.45) * mm});
            skLineSegment(sketch, "E431", {"start": v(15.87, -9.45) * mm, "end": v(16.5, -9.64) * mm});
            skLineSegment(sketch, "E432", {"start": v(16.5, -9.64) * mm, "end": v(16.87, -9.71) * mm});
            skLineSegment(sketch, "E433", {"start": v(16.87, -9.71) * mm, "end": v(17.48, -9.78) * mm});
            skLineSegment(sketch, "E434", {"start": v(17.48, -9.78) * mm, "end": v(18.32, -9.8) * mm});
            skLineSegment(sketch, "E435", {"start": v(18.32, -9.8) * mm, "end": v(19.4, -9.72) * mm});
            skLineSegment(sketch, "E436", {"start": v(19.4, -9.72) * mm, "end": v(20.37, -9.56) * mm});
            skLineSegment(sketch, "E437", {"start": v(-9.52, -1.96) * mm, "end": v(-9.94, -2) * mm});
            skLineSegment(sketch, "E438", {"start": v(-9.94, -2) * mm, "end": v(-10.35, -1.96) * mm});
            skLineSegment(sketch, "E439", {"start": v(-10.35, -1.96) * mm, "end": v(-10.75, -1.83) * mm});
            skLineSegment(sketch, "E440", {"start": v(-10.75, -1.83) * mm, "end": v(-11.11, -1.62) * mm});
            skLineSegment(sketch, "E441", {"start": v(-11.11, -1.62) * mm, "end": v(-11.42, -1.34) * mm});
            skLineSegment(sketch, "E442", {"start": v(-11.42, -1.34) * mm, "end": v(-11.67, -1) * mm});
            skLineSegment(sketch, "E443", {"start": v(-11.67, -1) * mm, "end": v(-11.84, -0.62) * mm});
            skLineSegment(sketch, "E444", {"start": v(-11.84, -0.62) * mm, "end": v(-11.92, -0.2) * mm});
            skLineSegment(sketch, "E445", {"start": v(-11.92, -0.2) * mm, "end": v(-11.92, 0.2) * mm});
            skLineSegment(sketch, "E446", {"start": v(-11.92, 0.2) * mm, "end": v(-11.84, 0.62) * mm});
            skLineSegment(sketch, "E447", {"start": v(-11.84, 0.62) * mm, "end": v(-11.67, 1) * mm});
            skLineSegment(sketch, "E448", {"start": v(-11.67, 1) * mm, "end": v(-11.42, 1.34) * mm});
            skLineSegment(sketch, "E449", {"start": v(-11.42, 1.34) * mm, "end": v(-11.11, 1.62) * mm});
            skLineSegment(sketch, "E450", {"start": v(-11.11, 1.62) * mm, "end": v(-10.75, 1.83) * mm});
            skLineSegment(sketch, "E451", {"start": v(-10.75, 1.83) * mm, "end": v(-10.35, 1.96) * mm});
            skLineSegment(sketch, "E452", {"start": v(-10.35, 1.96) * mm, "end": v(-9.94, 2) * mm});
            skLineSegment(sketch, "E453", {"start": v(-9.94, 2) * mm, "end": v(-9.52, 1.96) * mm});
            skLineSegment(sketch, "E454", {"start": v(-9.52, 1.96) * mm, "end": v(-9.12, 1.83) * mm});
            skLineSegment(sketch, "E455", {"start": v(-9.12, 1.83) * mm, "end": v(-8.76, 1.62) * mm});
            skLineSegment(sketch, "E456", {"start": v(-8.76, 1.62) * mm, "end": v(-8.45, 1.34) * mm});
            skLineSegment(sketch, "E457", {"start": v(-8.45, 1.34) * mm, "end": v(-8.2, 1) * mm});
            skLineSegment(sketch, "E458", {"start": v(-8.2, 1) * mm, "end": v(-8.03, 0.62) * mm});
            skLineSegment(sketch, "E459", {"start": v(-8.03, 0.62) * mm, "end": v(-7.95, 0.2) * mm});
            skLineSegment(sketch, "E460", {"start": v(-7.95, 0.2) * mm, "end": v(-7.95, -0.2) * mm});
            skLineSegment(sketch, "E461", {"start": v(-7.95, -0.2) * mm, "end": v(-8.03, -0.62) * mm});
            skLineSegment(sketch, "E462", {"start": v(-8.03, -0.62) * mm, "end": v(-8.2, -1) * mm});
            skLineSegment(sketch, "E463", {"start": v(-8.2, -1) * mm, "end": v(-8.45, -1.34) * mm});
            skLineSegment(sketch, "E464", {"start": v(-8.45, -1.34) * mm, "end": v(-8.76, -1.62) * mm});
            skLineSegment(sketch, "E465", {"start": v(-8.76, -1.62) * mm, "end": v(-9.12, -1.83) * mm});
            skLineSegment(sketch, "E466", {"start": v(-9.12, -1.83) * mm, "end": v(-9.52, -1.96) * mm});
            skLineSegment(sketch, "E467", {"start": v(18.16, 5.6) * mm, "end": v(17.77, 4.87) * mm});
            skLineSegment(sketch, "E468", {"start": v(17.77, 4.87) * mm, "end": v(17.53, 4.07) * mm});
            skLineSegment(sketch, "E469", {"start": v(17.53, 4.07) * mm, "end": v(17.77, 3.62) * mm});
            skLineSegment(sketch, "E470", {"start": v(17.77, 3.62) * mm, "end": v(18.87, 2.43) * mm});
            skLineSegment(sketch, "E471", {"start": v(18.87, 2.43) * mm, "end": v(19.68, 1.92) * mm});
            skLineSegment(sketch, "E472", {"start": v(19.68, 1.92) * mm, "end": v(19.95, 1.84) * mm});
            skLineSegment(sketch, "E473", {"start": v(19.95, 1.84) * mm, "end": v(21.2, 1.8) * mm});
            skLineSegment(sketch, "E474", {"start": v(21.2, 1.8) * mm, "end": v(21.95, 1.22) * mm});
            skLineSegment(sketch, "E475", {"start": v(21.95, 1.22) * mm, "end": v(21.95, -1.22) * mm});
            skLineSegment(sketch, "E476", {"start": v(21.95, -1.22) * mm, "end": v(21.2, -1.8) * mm});
            skLineSegment(sketch, "E477", {"start": v(21.2, -1.8) * mm, "end": v(19.95, -1.84) * mm});
            skLineSegment(sketch, "E478", {"start": v(19.95, -1.84) * mm, "end": v(19.68, -1.92) * mm});
            skLineSegment(sketch, "E479", {"start": v(19.68, -1.92) * mm, "end": v(18.87, -2.43) * mm});
            skLineSegment(sketch, "E480", {"start": v(18.87, -2.43) * mm, "end": v(17.77, -3.62) * mm});
            skLineSegment(sketch, "E481", {"start": v(17.77, -3.62) * mm, "end": v(17.53, -4.07) * mm});
            skLineSegment(sketch, "E482", {"start": v(17.53, -4.07) * mm, "end": v(17.77, -4.87) * mm});
            skLineSegment(sketch, "E483", {"start": v(17.77, -4.87) * mm, "end": v(18.16, -5.6) * mm});
            skLineSegment(sketch, "E484", {"start": v(18.16, -5.6) * mm, "end": v(18.65, -5.76) * mm});
            skLineSegment(sketch, "E485", {"start": v(18.65, -5.76) * mm, "end": v(20.28, -5.82) * mm});
            skLineSegment(sketch, "E486", {"start": v(20.28, -5.82) * mm, "end": v(21.2, -5.6) * mm});
            skLineSegment(sketch, "E487", {"start": v(21.2, -5.6) * mm, "end": v(21.45, -5.48) * mm});
            skLineSegment(sketch, "E488", {"start": v(21.45, -5.48) * mm, "end": v(22.37, -4.63) * mm});
            skLineSegment(sketch, "E489", {"start": v(22.37, -4.63) * mm, "end": v(23.3, -4.5) * mm});
            skLineSegment(sketch, "E490", {"start": v(23.3, -4.5) * mm, "end": v(25.03, -6.23) * mm});
            skLineSegment(sketch, "E491", {"start": v(25.03, -6.23) * mm, "end": v(24.9, -7.16) * mm});
            skLineSegment(sketch, "E492", {"start": v(24.9, -7.16) * mm, "end": v(24.06, -8.08) * mm});
            skLineSegment(sketch, "E493", {"start": v(24.06, -8.08) * mm, "end": v(23.93, -8.33) * mm});
            skLineSegment(sketch, "E494", {"start": v(23.93, -8.33) * mm, "end": v(23.71, -9.26) * mm});
            skLineSegment(sketch, "E495", {"start": v(23.71, -9.26) * mm, "end": v(23.78, -10.88) * mm});
            skLineSegment(sketch, "E496", {"start": v(23.78, -10.88) * mm, "end": v(23.93, -11.37) * mm});
            skLineSegment(sketch, "E497", {"start": v(23.93, -11.37) * mm, "end": v(24.66, -11.76) * mm});
            skLineSegment(sketch, "E498", {"start": v(24.66, -11.76) * mm, "end": v(25.46, -12) * mm});
            skLineSegment(sketch, "E499", {"start": v(25.46, -12) * mm, "end": v(25.91, -11.77) * mm});
            skLineSegment(sketch, "E500", {"start": v(25.91, -11.77) * mm, "end": v(27.1, -10.66) * mm});
            skLineSegment(sketch, "E501", {"start": v(27.1, -10.66) * mm, "end": v(27.61, -9.86) * mm});
            skLineSegment(sketch, "E502", {"start": v(27.61, -9.86) * mm, "end": v(27.7, -9.59) * mm});
            skLineSegment(sketch, "E503", {"start": v(27.7, -9.59) * mm, "end": v(27.74, -8.34) * mm});
            skLineSegment(sketch, "E504", {"start": v(27.74, -8.34) * mm, "end": v(28.31, -7.59) * mm});
            skLineSegment(sketch, "E505", {"start": v(28.31, -7.59) * mm, "end": v(30.76, -7.59) * mm});
            skLineSegment(sketch, "E506", {"start": v(30.76, -7.59) * mm, "end": v(31.33, -8.34) * mm});
            skLineSegment(sketch, "E507", {"start": v(31.33, -8.34) * mm, "end": v(31.38, -9.59) * mm});
            skLineSegment(sketch, "E508", {"start": v(31.38, -9.59) * mm, "end": v(31.46, -9.86) * mm});
            skLineSegment(sketch, "E509", {"start": v(31.46, -9.86) * mm, "end": v(31.97, -10.66) * mm});
            skLineSegment(sketch, "E510", {"start": v(31.97, -10.66) * mm, "end": v(33.16, -11.77) * mm});
            skLineSegment(sketch, "E511", {"start": v(33.16, -11.77) * mm, "end": v(33.6, -12) * mm});
            skLineSegment(sketch, "E512", {"start": v(33.6, -12) * mm, "end": v(34.4, -11.76) * mm});
            skLineSegment(sketch, "E513", {"start": v(34.4, -11.76) * mm, "end": v(35.14, -11.37) * mm});
            skLineSegment(sketch, "E514", {"start": v(35.14, -11.37) * mm, "end": v(35.3, -10.88) * mm});
            skLineSegment(sketch, "E515", {"start": v(35.3, -10.88) * mm, "end": v(35.36, -9.26) * mm});
            skLineSegment(sketch, "E516", {"start": v(35.36, -9.26) * mm, "end": v(35.14, -8.33) * mm});
            skLineSegment(sketch, "E517", {"start": v(35.14, -8.33) * mm, "end": v(35.01, -8.08) * mm});
            skLineSegment(sketch, "E518", {"start": v(35.01, -8.08) * mm, "end": v(34.16, -7.16) * mm});
            skLineSegment(sketch, "E519", {"start": v(34.16, -7.16) * mm, "end": v(34.04, -6.23) * mm});
            skLineSegment(sketch, "E520", {"start": v(34.04, -6.23) * mm, "end": v(35.77, -4.5) * mm});
            skLineSegment(sketch, "E521", {"start": v(35.77, -4.5) * mm, "end": v(36.7, -4.63) * mm});
            skLineSegment(sketch, "E522", {"start": v(36.7, -4.63) * mm, "end": v(37.62, -5.48) * mm});
            skLineSegment(sketch, "E523", {"start": v(37.62, -5.48) * mm, "end": v(37.87, -5.6) * mm});
            skLineSegment(sketch, "E524", {"start": v(37.87, -5.6) * mm, "end": v(38.8, -5.82) * mm});
            skLineSegment(sketch, "E525", {"start": v(38.8, -5.82) * mm, "end": v(40.42, -5.76) * mm});
            skLineSegment(sketch, "E526", {"start": v(40.42, -5.76) * mm, "end": v(40.9, -5.6) * mm});
            skLineSegment(sketch, "E527", {"start": v(40.9, -5.6) * mm, "end": v(41.3, -4.87) * mm});
            skLineSegment(sketch, "E528", {"start": v(41.3, -4.87) * mm, "end": v(41.54, -4.07) * mm});
            skLineSegment(sketch, "E529", {"start": v(41.54, -4.07) * mm, "end": v(41.3, -3.62) * mm});
            skLineSegment(sketch, "E530", {"start": v(41.3, -3.62) * mm, "end": v(40.2, -2.43) * mm});
            skLineSegment(sketch, "E531", {"start": v(40.2, -2.43) * mm, "end": v(39.4, -1.92) * mm});
            skLineSegment(sketch, "E532", {"start": v(39.4, -1.92) * mm, "end": v(39.12, -1.84) * mm});
            skLineSegment(sketch, "E533", {"start": v(39.12, -1.84) * mm, "end": v(37.87, -1.8) * mm});
            skLineSegment(sketch, "E534", {"start": v(37.87, -1.8) * mm, "end": v(37.12, -1.22) * mm});
            skLineSegment(sketch, "E535", {"start": v(37.12, -1.22) * mm, "end": v(37.12, 1.22) * mm});
            skLineSegment(sketch, "E536", {"start": v(37.12, 1.22) * mm, "end": v(37.87, 1.8) * mm});
            skLineSegment(sketch, "E537", {"start": v(37.87, 1.8) * mm, "end": v(39.12, 1.84) * mm});
            skLineSegment(sketch, "E538", {"start": v(39.12, 1.84) * mm, "end": v(39.4, 1.92) * mm});
            skLineSegment(sketch, "E539", {"start": v(39.4, 1.92) * mm, "end": v(40.2, 2.43) * mm});
            skLineSegment(sketch, "E540", {"start": v(40.2, 2.43) * mm, "end": v(41.3, 3.62) * mm});
            skLineSegment(sketch, "E541", {"start": v(41.3, 3.62) * mm, "end": v(41.54, 4.07) * mm});
            skLineSegment(sketch, "E542", {"start": v(41.54, 4.07) * mm, "end": v(41.3, 4.87) * mm});
            skLineSegment(sketch, "E543", {"start": v(41.3, 4.87) * mm, "end": v(40.9, 5.6) * mm});
            skLineSegment(sketch, "E544", {"start": v(40.9, 5.6) * mm, "end": v(40.42, 5.76) * mm});
            skLineSegment(sketch, "E545", {"start": v(40.42, 5.76) * mm, "end": v(38.8, 5.82) * mm});
            skLineSegment(sketch, "E546", {"start": v(38.8, 5.82) * mm, "end": v(37.87, 5.6) * mm});
            skLineSegment(sketch, "E547", {"start": v(37.87, 5.6) * mm, "end": v(37.62, 5.48) * mm});
            skLineSegment(sketch, "E548", {"start": v(37.62, 5.48) * mm, "end": v(36.7, 4.63) * mm});
            skLineSegment(sketch, "E549", {"start": v(36.7, 4.63) * mm, "end": v(35.77, 4.5) * mm});
            skLineSegment(sketch, "E550", {"start": v(35.77, 4.5) * mm, "end": v(34.04, 6.23) * mm});
            skLineSegment(sketch, "E551", {"start": v(34.04, 6.23) * mm, "end": v(34.16, 7.16) * mm});
            skLineSegment(sketch, "E552", {"start": v(34.16, 7.16) * mm, "end": v(35.01, 8.08) * mm});
            skLineSegment(sketch, "E553", {"start": v(35.01, 8.08) * mm, "end": v(35.14, 8.33) * mm});
            skLineSegment(sketch, "E554", {"start": v(35.14, 8.33) * mm, "end": v(35.36, 9.26) * mm});
            skLineSegment(sketch, "E555", {"start": v(35.36, 9.26) * mm, "end": v(35.3, 10.88) * mm});
            skLineSegment(sketch, "E556", {"start": v(35.3, 10.88) * mm, "end": v(35.14, 11.37) * mm});
            skLineSegment(sketch, "E557", {"start": v(35.14, 11.37) * mm, "end": v(34.4, 11.76) * mm});
            skLineSegment(sketch, "E558", {"start": v(34.4, 11.76) * mm, "end": v(33.6, 12) * mm});
            skLineSegment(sketch, "E559", {"start": v(33.6, 12) * mm, "end": v(33.16, 11.77) * mm});
            skLineSegment(sketch, "E560", {"start": v(33.16, 11.77) * mm, "end": v(31.97, 10.66) * mm});
            skLineSegment(sketch, "E561", {"start": v(31.97, 10.66) * mm, "end": v(31.46, 9.86) * mm});
            skLineSegment(sketch, "E562", {"start": v(31.46, 9.86) * mm, "end": v(31.38, 9.59) * mm});
            skLineSegment(sketch, "E563", {"start": v(31.38, 9.59) * mm, "end": v(31.33, 8.34) * mm});
            skLineSegment(sketch, "E564", {"start": v(31.33, 8.34) * mm, "end": v(30.76, 7.59) * mm});
            skLineSegment(sketch, "E565", {"start": v(30.76, 7.59) * mm, "end": v(28.31, 7.59) * mm});
            skLineSegment(sketch, "E566", {"start": v(28.31, 7.59) * mm, "end": v(27.74, 8.34) * mm});
            skLineSegment(sketch, "E567", {"start": v(27.74, 8.34) * mm, "end": v(27.7, 9.59) * mm});
            skLineSegment(sketch, "E568", {"start": v(27.7, 9.59) * mm, "end": v(27.61, 9.86) * mm});
            skLineSegment(sketch, "E569", {"start": v(27.61, 9.86) * mm, "end": v(27.1, 10.66) * mm});
            skLineSegment(sketch, "E570", {"start": v(27.1, 10.66) * mm, "end": v(25.91, 11.77) * mm});
            skLineSegment(sketch, "E571", {"start": v(25.91, 11.77) * mm, "end": v(25.46, 12) * mm});
            skLineSegment(sketch, "E572", {"start": v(25.46, 12) * mm, "end": v(24.66, 11.76) * mm});
            skLineSegment(sketch, "E573", {"start": v(24.66, 11.76) * mm, "end": v(23.93, 11.37) * mm});
            skLineSegment(sketch, "E574", {"start": v(23.93, 11.37) * mm, "end": v(23.78, 10.88) * mm});
            skLineSegment(sketch, "E575", {"start": v(23.78, 10.88) * mm, "end": v(23.71, 9.26) * mm});
            skLineSegment(sketch, "E576", {"start": v(23.71, 9.26) * mm, "end": v(23.93, 8.33) * mm});
            skLineSegment(sketch, "E577", {"start": v(23.93, 8.33) * mm, "end": v(24.06, 8.08) * mm});
            skLineSegment(sketch, "E578", {"start": v(24.06, 8.08) * mm, "end": v(24.9, 7.16) * mm});
            skLineSegment(sketch, "E579", {"start": v(24.9, 7.16) * mm, "end": v(25.03, 6.23) * mm});
            skLineSegment(sketch, "E580", {"start": v(25.03, 6.23) * mm, "end": v(23.3, 4.5) * mm});
            skLineSegment(sketch, "E581", {"start": v(23.3, 4.5) * mm, "end": v(22.37, 4.63) * mm});
            skLineSegment(sketch, "E582", {"start": v(22.37, 4.63) * mm, "end": v(21.45, 5.48) * mm});
            skLineSegment(sketch, "E583", {"start": v(21.45, 5.48) * mm, "end": v(21.2, 5.6) * mm});
            skLineSegment(sketch, "E584", {"start": v(21.2, 5.6) * mm, "end": v(20.28, 5.82) * mm});
            skLineSegment(sketch, "E585", {"start": v(20.28, 5.82) * mm, "end": v(18.65, 5.76) * mm});
            skLineSegment(sketch, "E586", {"start": v(18.65, 5.76) * mm, "end": v(18.16, 5.6) * mm});
            skLineSegment(sketch, "E587", {"start": v(28.4, 1.65) * mm, "end": v(28.77, 1.85) * mm});
            skLineSegment(sketch, "E588", {"start": v(28.77, 1.85) * mm, "end": v(29.17, 1.97) * mm});
            skLineSegment(sketch, "E589", {"start": v(29.17, 1.97) * mm, "end": v(29.59, 2) * mm});
            skLineSegment(sketch, "E590", {"start": v(29.59, 2) * mm, "end": v(30, 1.94) * mm});
            skLineSegment(sketch, "E591", {"start": v(30, 1.94) * mm, "end": v(30.4, 1.8) * mm});
            skLineSegment(sketch, "E592", {"start": v(30.4, 1.8) * mm, "end": v(30.75, 1.59) * mm});
            skLineSegment(sketch, "E593", {"start": v(30.75, 1.59) * mm, "end": v(31.06, 1.3) * mm});
            skLineSegment(sketch, "E594", {"start": v(31.06, 1.3) * mm, "end": v(31.3, 0.95) * mm});
            skLineSegment(sketch, "E595", {"start": v(31.3, 0.95) * mm, "end": v(31.45, 0.57) * mm});
            skLineSegment(sketch, "E596", {"start": v(31.45, 0.57) * mm, "end": v(31.53, 0.16) * mm});
            skLineSegment(sketch, "E597", {"start": v(31.53, 0.16) * mm, "end": v(31.52, -0.26) * mm});
            skLineSegment(sketch, "E598", {"start": v(31.52, -0.26) * mm, "end": v(31.42, -0.67) * mm});
            skLineSegment(sketch, "E599", {"start": v(31.42, -0.67) * mm, "end": v(31.24, -1.04) * mm});
            skLineSegment(sketch, "E600", {"start": v(31.24, -1.04) * mm, "end": v(30.99, -1.38) * mm});
            skLineSegment(sketch, "E601", {"start": v(30.99, -1.38) * mm, "end": v(30.67, -1.65) * mm});
            skLineSegment(sketch, "E602", {"start": v(30.67, -1.65) * mm, "end": v(30.3, -1.85) * mm});
            skLineSegment(sketch, "E603", {"start": v(30.3, -1.85) * mm, "end": v(29.9, -1.97) * mm});
            skLineSegment(sketch, "E604", {"start": v(29.9, -1.97) * mm, "end": v(29.48, -2) * mm});
            skLineSegment(sketch, "E605", {"start": v(29.48, -2) * mm, "end": v(29.07, -1.94) * mm});
            skLineSegment(sketch, "E606", {"start": v(29.07, -1.94) * mm, "end": v(28.67, -1.8) * mm});
            skLineSegment(sketch, "E607", {"start": v(28.67, -1.8) * mm, "end": v(28.32, -1.59) * mm});
            skLineSegment(sketch, "E608", {"start": v(28.32, -1.59) * mm, "end": v(28.01, -1.3) * mm});
            skLineSegment(sketch, "E609", {"start": v(28.01, -1.3) * mm, "end": v(27.78, -0.95) * mm});
            skLineSegment(sketch, "E610", {"start": v(27.78, -0.95) * mm, "end": v(27.62, -0.57) * mm});
            skLineSegment(sketch, "E611", {"start": v(27.62, -0.57) * mm, "end": v(27.54, -0.16) * mm});
            skLineSegment(sketch, "E612", {"start": v(27.54, -0.16) * mm, "end": v(27.55, 0.26) * mm});
            skLineSegment(sketch, "E613", {"start": v(27.55, 0.26) * mm, "end": v(27.65, 0.67) * mm});
            skLineSegment(sketch, "E614", {"start": v(27.65, 0.67) * mm, "end": v(27.83, 1.04) * mm});
            skLineSegment(sketch, "E615", {"start": v(27.83, 1.04) * mm, "end": v(28.08, 1.38) * mm});
            skLineSegment(sketch, "E616", {"start": v(28.08, 1.38) * mm, "end": v(28.4, 1.65) * mm});
            skSolve(sketch);
        }
        {
            var Q0;
            Q0=qCreatedBy(makeId("Top.planeOp"),FACE);
            var sketch = newSketch(context, id + "F1", { "sketchPlane" : qUnion([Q0])});
            skCircle(sketch, "E617", {"center": v(-23.85, 0) * mm, "radius": 8.5 * mm});
            skCircle(sketch, "E618", {"center": v(-9.85, 14) * mm, "radius": 8.5 * mm});
            skCircle(sketch, "E619", {"center": v(4.15, 0) * mm, "radius": 8.5 * mm});
            skCircle(sketch, "E620", {"center": v(-9.85, -14) * mm, "radius": 8.5 * mm});
            skSolve(sketch);
        }
        {
            var Q0;
            Q0=makeQuery(id+"F0.imprint","IMPRINT",FACE,{"disambiguationData":[TD([[makeQuery(id+"F0.imprint","IMPRINT",EDGE,{"derivedFrom":sQuery(id+"F0.wireOp",EDGE,"E0")}),1.0]])]});
            extrude(context, id + "F2", {"entities" : qUnion([Q0]), "depth" : 7 * mm});
        }
        {
            var Q0;
            Q0=qSketchRegion(id+"F1",true);
            extrude(context, id + "F3", {"entities" : qUnion([Q0]), "operationType" : NewBodyOperationType.REMOVE, "endBound" : BoundingType.SYMMETRIC, "oppositeDirection" : true, "depth" : 25 * mm});
        }
    });
